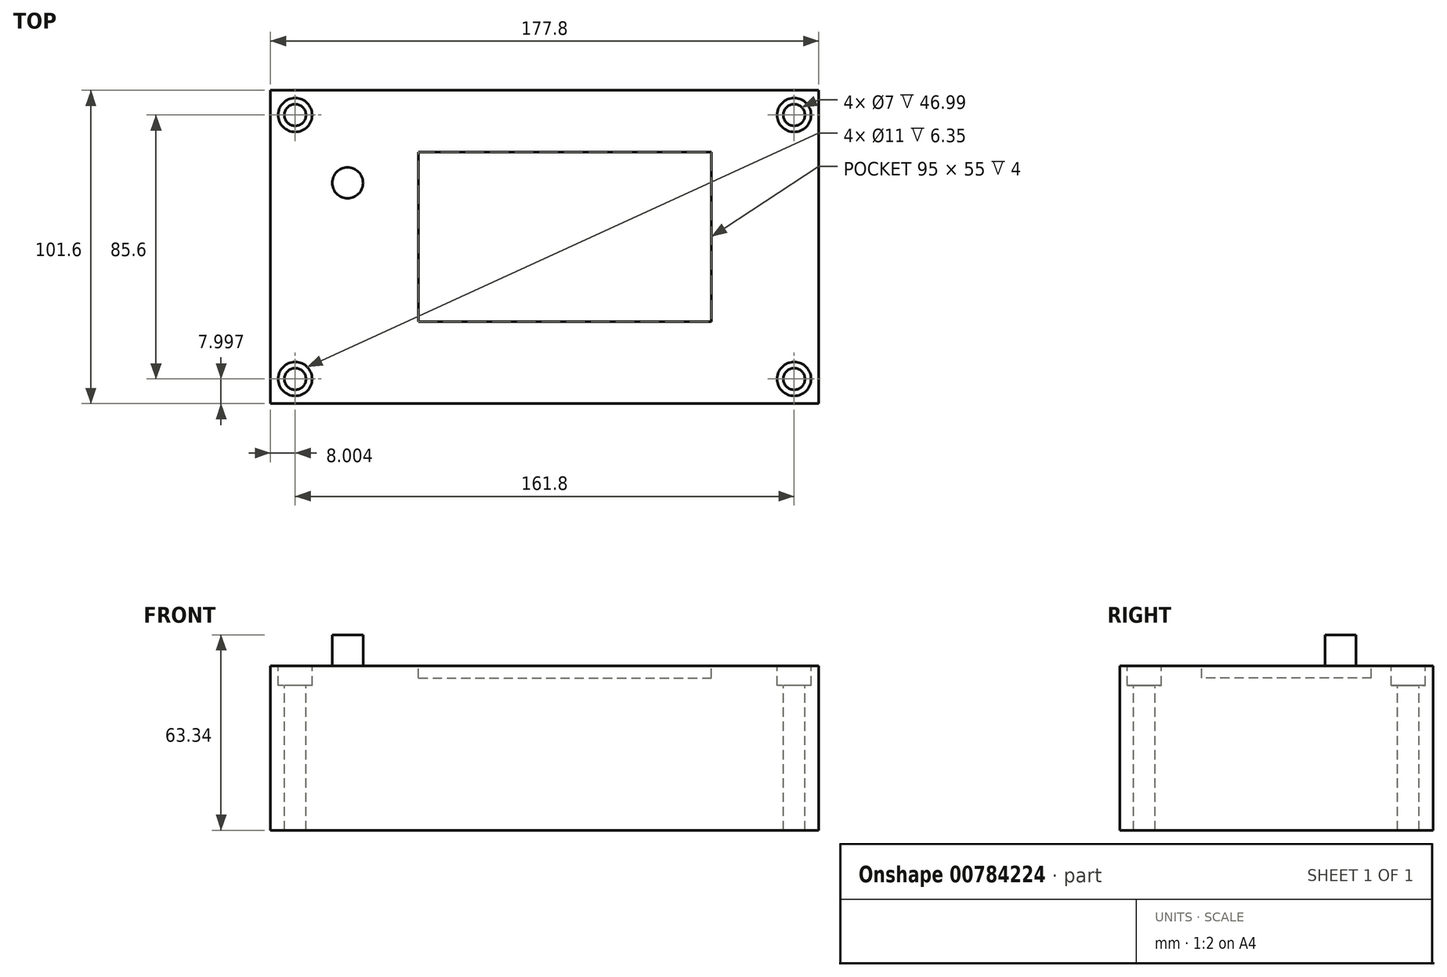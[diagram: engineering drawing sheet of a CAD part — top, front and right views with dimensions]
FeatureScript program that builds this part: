
annotation { "Feature Type Name" : "Feature", "Feature Type Description" : "" }
export const myFeature = defineFeature(function(context is Context, id is Id, definition is map)
    precondition{}
    {
        {
            var Q0;
            Q0=qCreatedBy(makeId("Top.planeOp"),FACE);
            var sketch = newSketch(context, id + "F0", { "sketchPlane" : qUnion([Q0])});
            skLineSegment(sketch, "E0.bottom", {"start": v(-88.62, 57.95) * mm, "end": v(89.18, 57.95) * mm});
            skLineSegment(sketch, "E0.top", {"start": v(-88.62, -43.65) * mm, "end": v(89.18, -43.65) * mm});
            skLineSegment(sketch, "E0.left", {"start": v(-88.62, 57.95) * mm, "end": v(-88.62, -43.65) * mm});
            skLineSegment(sketch, "E0.right", {"start": v(89.18, 57.95) * mm, "end": v(89.18, -43.65) * mm});
            skSolve(sketch);
        }
        {
            var Q0;
            Q0=makeQuery(id+"F0.imprint","IMPRINT",FACE,{"disambiguationData":[TD([[makeQuery(id+"F0.imprint","IMPRINT",EDGE,{"derivedFrom":sQuery(id+"F0.wireOp",EDGE,"E0.bottom")}),-1.0]])]});
            extrude(context, id + "F1", {"entities" : qUnion([Q0]), "depth" : 53.34 * mm, "offsetDistance" : 25.4 * mm});
        }
        {
            var Q0;
            Q0=makeQuery(id+"F1.opExtrude","CAP_FACE",FACE,{"disambiguationData":[OSD([sQuery(id+"F0.wireOp",EDGE,"E0.bottom"),sQuery(id+"F0.wireOp",EDGE,"E0.top"),sQuery(id+"F0.wireOp",EDGE,"E0.left"),sQuery(id+"F0.wireOp",EDGE,"E0.right")])],"isStart":false});
            var sketch = newSketch(context, id + "F2", { "sketchPlane" : qUnion([Q0])});
            skPoint(sketch, "E1", {"position": v(-80.62, 49.95) * mm});
            skPoint(sketch, "E2", {"position": v(-80.62, -35.65) * mm});
            skPoint(sketch, "E3", {"position": v(81.18, -35.65) * mm});
            skPoint(sketch, "E4", {"position": v(81.18, 49.95) * mm});
            skCircle(sketch, "E5", {"center": v(-63.62, 27.95) * mm, "radius": 5 * mm});
            skLineSegment(sketch, "E6.bottom", {"start": v(-40.62, 37.95) * mm, "end": v(54.38, 37.95) * mm});
            skLineSegment(sketch, "E6.top", {"start": v(-40.62, -17.05) * mm, "end": v(54.38, -17.05) * mm});
            skLineSegment(sketch, "E6.left", {"start": v(-40.62, 37.95) * mm, "end": v(-40.62, -17.05) * mm});
            skLineSegment(sketch, "E6.right", {"start": v(54.38, 37.95) * mm, "end": v(54.38, -17.05) * mm});
            skSolve(sketch);
        }
        {
            var Q0;
            Q0=makeQuery(id+"F2.imprint","IMPRINT",FACE,{"disambiguationData":[TD([[makeQuery(id+"F2.imprint","IMPRINT",EDGE,{"derivedFrom":sQuery(id+"F2.wireOp",EDGE,"E6.bottom")}),-1.0]])]});
            extrude(context, id + "F3", {"entities" : qUnion([Q0]), "operationType" : NewBodyOperationType.REMOVE, "oppositeDirection" : true, "depth" : 4 * mm, "offsetDistance" : 25.4 * mm});
        }
        {
            var Q0;
            Q0=sQuery(id+"F2.wireOp",VERTEX,"E1");
            var Q1;
            Q1=sQuery(id+"F2.wireOp",VERTEX,"E2");
            var Q2;
            Q2=sQuery(id+"F2.wireOp",VERTEX,"E3");
            var Q3;
            Q3=sQuery(id+"F2.wireOp",VERTEX,"E4");
            var Q4;
            Q4=makeQuery(id+"F1.opExtrude","SWEPT_BODY",BODY,{"disambiguationData":[OSD([sQuery(id+"F0.wireOp",EDGE,"E0.bottom"),sQuery(id+"F0.wireOp",EDGE,"E0.top"),sQuery(id+"F0.wireOp",EDGE,"E0.left"),sQuery(id+"F0.wireOp",EDGE,"E0.right")])]});
            hole(context, id + "F4", {"style" : HoleStyle.C_BORE, "endStyle" : HoleEndStyle.THROUGH, "holeDiameter" : 7 * mm, "cBoreDiameter" : 11 * mm, "cBoreDepth" : 6.35 * mm, "majorDiameter" : 6.35 * mm, "isTappedThrough" : true, "tappedDepth" : 12.7 * mm, "tapClearance" : 3, "locations" : qUnion([Q0, Q1, Q2, Q3]), "scope" : qUnion([Q4])});
        }
        {
            var Q0;
            Q0=makeQuery(id+"F2.imprint","IMPRINT",FACE,{"disambiguationData":[TD([[makeQuery(id+"F2.imprint","IMPRINT",EDGE,{"derivedFrom":sQuery(id+"F2.wireOp",EDGE,"E5")}),1.0]])]});
            extrude(context, id + "F5", {"entities" : qUnion([Q0]), "operationType" : NewBodyOperationType.ADD, "depth" : 10 * mm, "offsetDistance" : 25.4 * mm});
        }
    });
